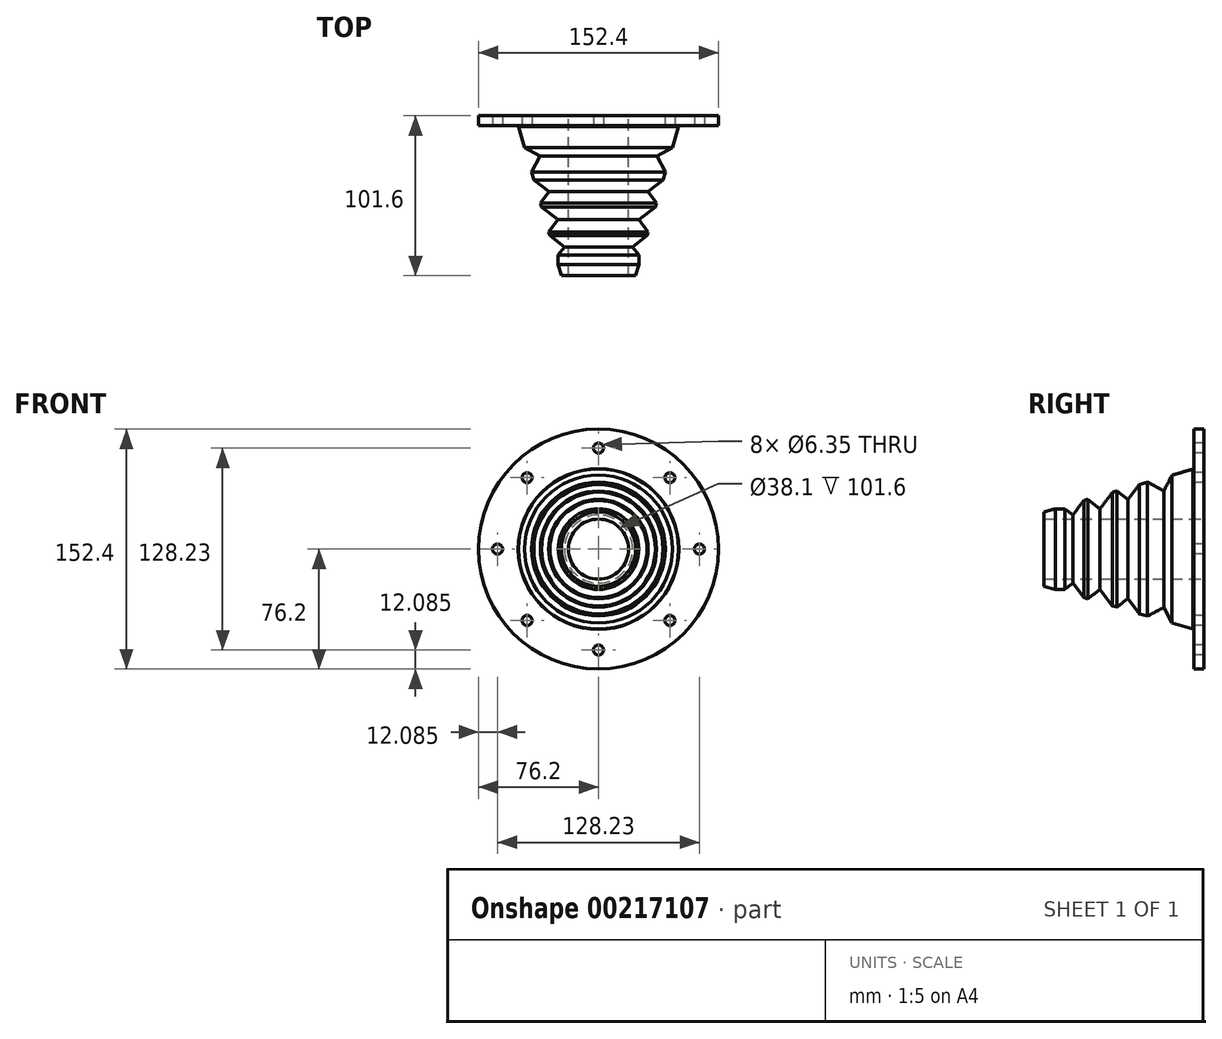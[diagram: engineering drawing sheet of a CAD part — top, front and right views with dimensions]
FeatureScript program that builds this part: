
annotation { "Feature Type Name" : "Feature", "Feature Type Description" : "" }
export const myFeature = defineFeature(function(context is Context, id is Id, definition is map)
    precondition{}
    {
        {
            var Q0;
            Q0=qCreatedBy(makeId("Front.planeOp"),FACE);
            var sketch = newSketch(context, id + "F0", { "sketchPlane" : qUnion([Q0])});
            skCircle(sketch, "E0", {"center": v(0, 0) * mm, "radius": 19.05 * mm});
            skCircle(sketch, "E1", {"center": v(0, 0) * mm, "radius": 50.8 * mm});
            skCircle(sketch, "E2", {"center": v(0, 0) * mm, "radius": 76.2 * mm});
            skSolve(sketch);
        }
        {
            var Q0;
            Q0=makeQuery(id+"F0.imprint","IMPRINT",FACE,{"disambiguationData":[TD([[makeQuery(id+"F0.imprint","IMPRINT",EDGE,{"derivedFrom":sQuery(id+"F0.wireOp",EDGE,"E0")}),-1.0]])]});
            extrude(context, id + "F1", {"entities" : qUnion([Q0]), "depth" : 101.6 * mm});
        }
        {
            var Q0;
            Q0=makeQuery(id+"F0.imprint","IMPRINT",FACE,{"disambiguationData":[TD([[makeQuery(id+"F0.imprint","IMPRINT",EDGE,{"derivedFrom":sQuery(id+"F0.wireOp",EDGE,"E1")}),-1.0]])]});
            extrude(context, id + "F2", {"entities" : qUnion([Q0]), "operationType" : NewBodyOperationType.ADD, "depth" : 6.35 * mm});
        }
        {
            var Q0;
            Q0=qCreatedBy(makeId("Right.planeOp"),FACE);
            var sketch = newSketch(context, id + "F3", { "sketchPlane" : qUnion([Q0])});
            skLineSegment(sketch, "E3", {"start": v(0, 50.98) * mm, "end": v(-6.34, 50.98) * mm});
            skLineSegment(sketch, "E4", {"start": v(-6.34, 50.98) * mm, "end": v(-109.35, 21.37) * mm});
            skLineSegment(sketch, "E5", {"start": v(-109.35, 21.37) * mm, "end": v(-107.68, 54.31) * mm});
            skLineSegment(sketch, "E6", {"start": v(-107.68, 54.31) * mm, "end": v(-6.34, 50.98) * mm});
            skSolve(sketch);
        }
        {
            var Q0;
            Q0=makeQuery(id+"F3.imprint","IMPRINT",FACE,{"disambiguationData":[TD([[makeQuery(id+"F3.imprint","IMPRINT",EDGE,{"derivedFrom":sQuery(id+"F3.wireOp",EDGE,"E4")}),-1.0]])]});
            var Q1;
            Q1=makeQuery(id+"F1.opExtrude","CAP_EDGE",EDGE,{"disambiguationData":[OSD([sQuery(id+"F0.wireOp",EDGE,"E1")])],"isStart":false});
            revolve(context, id + "F4", {"operationType" : NewBodyOperationType.REMOVE, "entities" : qUnion([Q0]), "axis" : qUnion([Q1]), "revolveType" : RevolveType.FULL, "oppositeDirection" : true});
        }
        {
            var Q0;
            Q0=qCreatedBy(makeId("Top.planeOp"),FACE);
            var sketch = newSketch(context, id + "F5", { "sketchPlane" : qUnion([Q0])});
            skLineSegment(sketch, "E7", {"start": v(-25.63, -95.7) * mm, "end": v(-25.63, -88.51) * mm});
            skLineSegment(sketch, "E8", {"start": v(-25.63, -88.51) * mm, "end": v(-21.66, -83.3) * mm});
            skLineSegment(sketch, "E9", {"start": v(-21.66, -83.3) * mm, "end": v(-32.5, -75.05) * mm});
            skLineSegment(sketch, "E10", {"start": v(-32.5, -75.05) * mm, "end": v(-25.63, -66.02) * mm});
            skLineSegment(sketch, "E11", {"start": v(-25.63, -66.02) * mm, "end": v(-37.85, -56.71) * mm});
            skLineSegment(sketch, "E12", {"start": v(-37.85, -56.71) * mm, "end": v(-31.4, -48.24) * mm});
            skLineSegment(sketch, "E13", {"start": v(-31.4, -48.24) * mm, "end": v(-43.97, -38.66) * mm});
            skLineSegment(sketch, "E14", {"start": v(-43.97, -38.66) * mm, "end": v(-37.04, -25.53) * mm});
            skLineSegment(sketch, "E15", {"start": v(-37.04, -25.53) * mm, "end": v(-49.32, -19.04) * mm});
            skLineSegment(sketch, "E16", {"start": v(-49.32, -19.04) * mm, "end": v(-52.41, -6.68) * mm});
            skLineSegment(sketch, "E17", {"start": v(-52.41, -6.68) * mm, "end": v(-55.39, -52.06) * mm});
            skLineSegment(sketch, "E18", {"start": v(-55.39, -52.06) * mm, "end": v(-25.63, -95.7) * mm});
            skSolve(sketch);
        }
        {
            var Q0;
            Q0=makeQuery(id+"F5.imprint","IMPRINT",FACE,{"disambiguationData":[TD([[makeQuery(id+"F5.imprint","IMPRINT",EDGE,{"derivedFrom":sQuery(id+"F5.wireOp",EDGE,"E7")}),1.0]])]});
            var Q1;
            Q1=makeQuery(id+"F4.boolean.opBoolean","INTERSECT",EDGE,{"derivedFrom":[makeQuery(id+"F1.opExtrude","CAP_FACE",FACE,{"disambiguationData":[OSD([sQuery(id+"F0.wireOp",EDGE,"E0"),sQuery(id+"F0.wireOp",EDGE,"E1")])],"isStart":false}),makeQuery(id+"F4.opRevolve","SWEPT_FACE",FACE,{"disambiguationData":[OSD([sQuery(id+"F3.wireOp",EDGE,"E4")])]})]});
            revolve(context, id + "F6", {"operationType" : NewBodyOperationType.REMOVE, "entities" : qUnion([Q0]), "axis" : qUnion([Q1]), "revolveType" : RevolveType.FULL, "oppositeDirection" : true});
        }
        {
            var Q0;
            {var subQ0=sQuery(id+"F0.wireOp",EDGE,"E2");Q0=makeQuery(id+"F4.boolean.opBoolean","SPLIT",FACE,{"disambiguationData":[TD([makeQuery(id+"F2.opExtrude","SWEPT_FACE",FACE,{"disambiguationData":[OSD([subQ0])]})])],"derivedFrom":makeQuery(id+"F2.opExtrude","CAP_FACE",FACE,{"disambiguationData":[OSD([sQuery(id+"F0.wireOp",EDGE,"E1"),subQ0])],"isStart":false})});}
            var sketch = newSketch(context, id + "F7", { "sketchPlane" : qUnion([Q0])});
            skCircle(sketch, "E19", {"center": v(0, 64.11) * mm, "radius": 3.18 * mm});
            skCircle(sketch, "E20.1.0", {"center": v(-45.34, 45.34) * mm, "radius": 3.18 * mm});
            skCircle(sketch, "E20.2.0", {"center": v(-64.11, 0) * mm, "radius": 3.18 * mm});
            skCircle(sketch, "E20.3.0", {"center": v(-45.34, -45.34) * mm, "radius": 3.18 * mm});
            skCircle(sketch, "E20.4.0", {"center": v(0, -64.11) * mm, "radius": 3.18 * mm});
            skCircle(sketch, "E20.5.0", {"center": v(45.34, -45.34) * mm, "radius": 3.18 * mm});
            skCircle(sketch, "E20.6.0", {"center": v(64.11, 0) * mm, "radius": 3.18 * mm});
            skCircle(sketch, "E20.7.0", {"center": v(45.34, 45.34) * mm, "radius": 3.18 * mm});
            skPoint(sketch, "E20.center", {"position": v(0, 0) * mm});
            skSolve(sketch);
        }
        {
            var Q0;
            Q0=makeQuery(id+"F7.imprint","IMPRINT",FACE,{"disambiguationData":[TD([[makeQuery(id+"F7.imprint","IMPRINT",EDGE,{"derivedFrom":sQuery(id+"F7.wireOp",EDGE,"E19")}),1.0]])]});
            var Q1;
            Q1=makeQuery(id+"F7.imprint","IMPRINT",FACE,{"disambiguationData":[TD([[makeQuery(id+"F7.imprint","IMPRINT",EDGE,{"derivedFrom":sQuery(id+"F7.wireOp",EDGE,"E20.7.0")}),1.0]])]});
            var Q2;
            Q2=makeQuery(id+"F7.imprint","IMPRINT",FACE,{"disambiguationData":[TD([[makeQuery(id+"F7.imprint","IMPRINT",EDGE,{"derivedFrom":sQuery(id+"F7.wireOp",EDGE,"E20.1.0")}),1.0]])]});
            var Q3;
            Q3=makeQuery(id+"F7.imprint","IMPRINT",FACE,{"disambiguationData":[TD([[makeQuery(id+"F7.imprint","IMPRINT",EDGE,{"derivedFrom":sQuery(id+"F7.wireOp",EDGE,"E20.2.0")}),1.0]])]});
            var Q4;
            Q4=makeQuery(id+"F7.imprint","IMPRINT",FACE,{"disambiguationData":[TD([[makeQuery(id+"F7.imprint","IMPRINT",EDGE,{"derivedFrom":sQuery(id+"F7.wireOp",EDGE,"E20.6.0")}),1.0]])]});
            var Q5;
            Q5=makeQuery(id+"F7.imprint","IMPRINT",FACE,{"disambiguationData":[TD([[makeQuery(id+"F7.imprint","IMPRINT",EDGE,{"derivedFrom":sQuery(id+"F7.wireOp",EDGE,"E20.5.0")}),1.0]])]});
            var Q6;
            Q6=makeQuery(id+"F7.imprint","IMPRINT",FACE,{"disambiguationData":[TD([[makeQuery(id+"F7.imprint","IMPRINT",EDGE,{"derivedFrom":sQuery(id+"F7.wireOp",EDGE,"E20.4.0")}),1.0]])]});
            var Q7;
            Q7=makeQuery(id+"F7.imprint","IMPRINT",FACE,{"disambiguationData":[TD([[makeQuery(id+"F7.imprint","IMPRINT",EDGE,{"derivedFrom":sQuery(id+"F7.wireOp",EDGE,"E20.3.0")}),1.0]])]});
            extrude(context, id + "F8", {"entities" : qUnion([Q0, Q1, Q2, Q3, Q4, Q5, Q6, Q7]), "operationType" : NewBodyOperationType.REMOVE, "oppositeDirection" : true, "depth" : 25.4 * mm});
        }
    });
